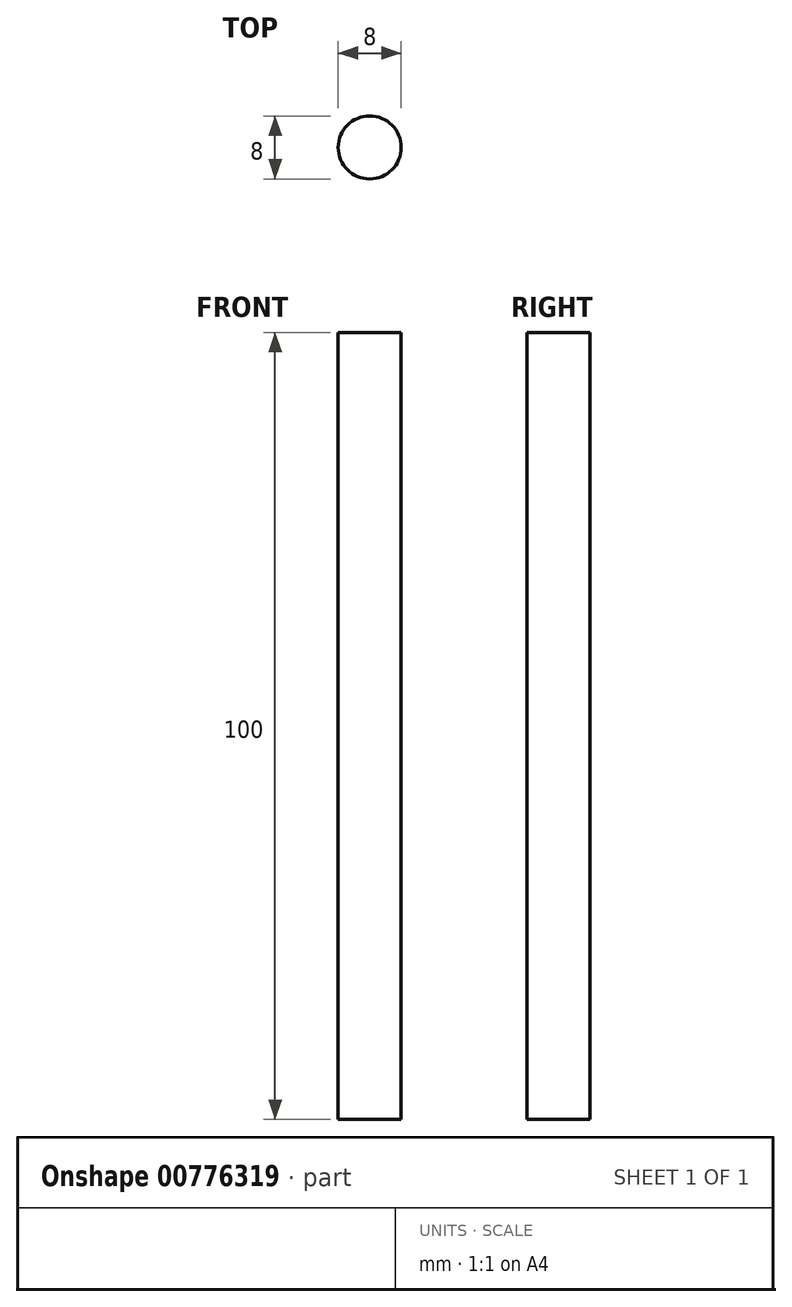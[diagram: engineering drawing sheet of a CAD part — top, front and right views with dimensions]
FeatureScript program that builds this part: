
annotation { "Feature Type Name" : "Feature", "Feature Type Description" : "" }
export const myFeature = defineFeature(function(context is Context, id is Id, definition is map)
    precondition{}
    {
        {
            var Q0;
            Q0=qCreatedBy(makeId("Top.planeOp"),FACE);
            var sketch = newSketch(context, id + "F0", { "sketchPlane" : qUnion([Q0])});
            skCircle(sketch, "E0", {"center": v(0, 0) * mm, "radius": 4 * mm});
            skSolve(sketch);
        }
        {
            var Q0;
            Q0=makeQuery(id+"F0.imprint","IMPRINT",FACE,{"disambiguationData":[TD([[makeQuery(id+"F0.imprint","IMPRINT",EDGE,{"derivedFrom":sQuery(id+"F0.wireOp",EDGE,"E0")}),1.0]])]});
            extrude(context, id + "F1", {"entities" : qUnion([Q0]), "depth" : 100 * mm, "offsetDistance" : 25 * mm});
        }
    });
